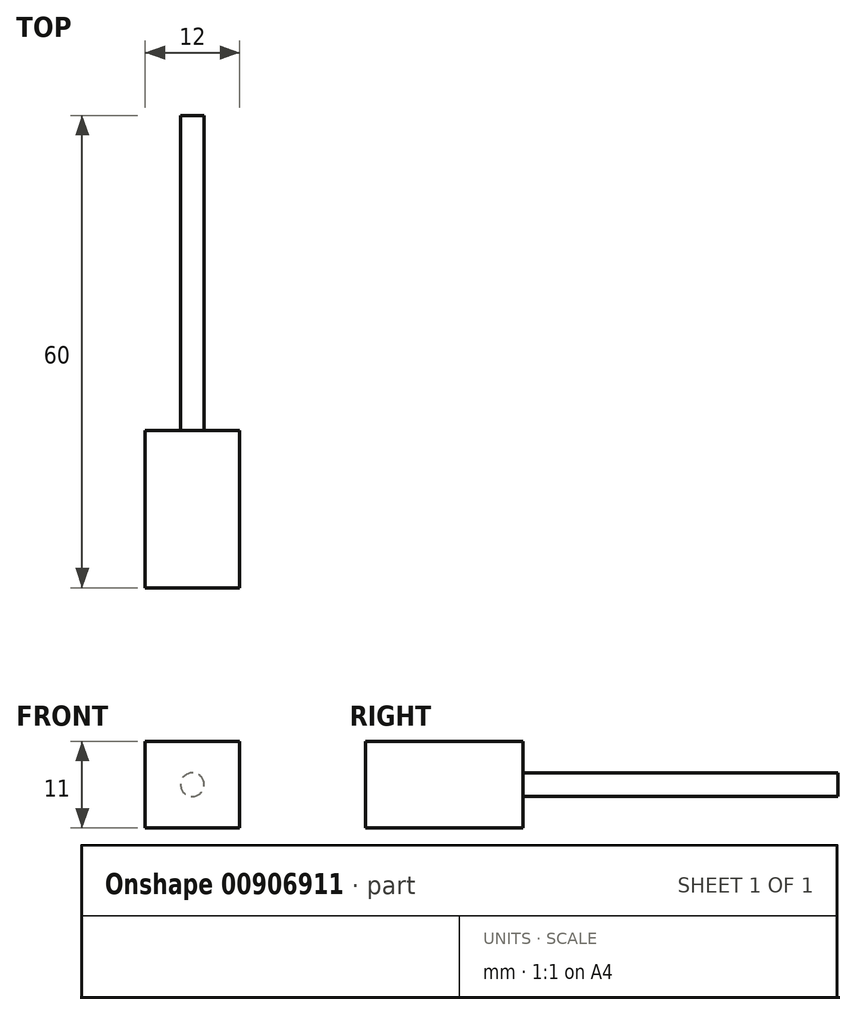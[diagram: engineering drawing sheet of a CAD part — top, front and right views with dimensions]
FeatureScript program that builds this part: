
annotation { "Feature Type Name" : "Feature", "Feature Type Description" : "" }
export const myFeature = defineFeature(function(context is Context, id is Id, definition is map)
    precondition{}
    {
        {
            var Q0;
            Q0=qCreatedBy(makeId("Top.planeOp"),FACE);
            var sketch = newSketch(context, id + "F0", { "sketchPlane" : qUnion([Q0])});
            skLineSegment(sketch, "E0.bottom", {"start": v(6, -10) * mm, "end": v(-6, -10) * mm});
            skLineSegment(sketch, "E0.top", {"start": v(6, 10) * mm, "end": v(-6, 10) * mm});
            skLineSegment(sketch, "E0.left", {"start": v(6, -10) * mm, "end": v(6, 10) * mm});
            skLineSegment(sketch, "E0.right", {"start": v(-6, -10) * mm, "end": v(-6, 10) * mm});
            skPoint(sketch, "E0.middle", {"position": v(0, 0) * mm});
            skSolve(sketch);
        }
        {
            var Q0;
            Q0=makeQuery(id+"F0.imprint","IMPRINT",FACE,{"disambiguationData":[TD([[makeQuery(id+"F0.imprint","IMPRINT",EDGE,{"derivedFrom":sQuery(id+"F0.wireOp",EDGE,"E0.bottom")}),-1.0]])]});
            extrude(context, id + "F1", {"entities" : qUnion([Q0]), "depth" : 11 * mm, "offsetDistance" : 25.4 * mm});
        }
        {
            var Q0;
            Q0=makeQuery(id+"F1.opExtrude","SWEPT_FACE",FACE,{"disambiguationData":[OSD([sQuery(id+"F0.wireOp",EDGE,"E0.top")])]});
            var sketch = newSketch(context, id + "F2", { "sketchPlane" : qUnion([Q0])});
            skCircle(sketch, "E1", {"center": v(0, 5.5) * mm, "radius": 1.5 * mm});
            skPoint(sketch, "E1.centerSnap0", {"position": v(-6, 5.5) * mm});
            skPoint(sketch, "E1.centerSnap1", {"position": v(0, 11) * mm});
            skSolve(sketch);
        }
        {
            var Q0;
            Q0=makeQuery(id+"F2.imprint","IMPRINT",FACE,{"disambiguationData":[TD([[makeQuery(id+"F2.imprint","IMPRINT",EDGE,{"derivedFrom":sQuery(id+"F2.wireOp",EDGE,"E1")}),1.0]])]});
            extrude(context, id + "F3", {"entities" : qUnion([Q0]), "operationType" : NewBodyOperationType.ADD, "depth" : 40 * mm, "offsetDistance" : 25.4 * mm});
        }
    });
